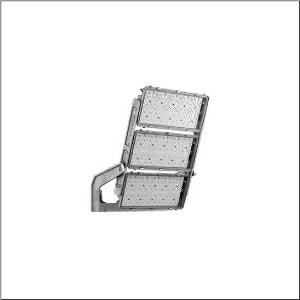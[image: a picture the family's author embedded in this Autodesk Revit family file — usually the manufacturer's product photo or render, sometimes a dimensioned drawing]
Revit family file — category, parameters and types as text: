
# Revit family: floodlight_fl_11_maxi_pro_remote___pl64_5xa779427v01aa_f124
name_source: partatom
category: Lighting Fixtures
units: mm (PartAtom-declared; Revit-internal decimal feet)

## family parameters
Cut with Voids When Loaded = No
Host = Face
Light Source = No
Part Type = Normal
Room Calculation Point = No
Round Connector Dimension = Use Diameter
Shared = No

## types (1)
- --- (1 x LED, 220410 lm, 1540.1 W, 5000K)
    Apparent Load = 1540 VA
    CIE Flux Codes = 28 79 98 100 100
    Color Rendering = 70
    Color Temperature = 5000K
    Default Elevation = 1800 mm
    Description = Floodlight FL 11  maxi  pro Remote floodlight; light control with lens of PMMA; cover panel of toughened safety glass, transparent; light distribution: PL64, asymmetric direct distribution, LEDcolour temperature: 5000K, rated luminous flux: 220.410lm, colour rendering: CRI > 70, light colour: 750; luminous efficacy: 143lm/W; brightness control: DALI 2 (1 DALI address); with terminal, 8-pole, max. 2.5mm², mains connection: 220..240V/380..400V AC, 50/60Hz, surge voltage resistance: line to ground: 10kV, ECG replaceable separately, no afterglow with DALI off / DMX off command, LED unit replaceable without ESD environment, dustproof LED module, dimming range 10..100%; 1540W floodlight with 2x LED unit of diecast aluminium, coated grey; length: 713mm / width: 651mm / height: 338mm; mounting bracket, of diecast aluminium, uncoated, natural, equipment: Power, protection rating (complete): IP66; insulation class (complete): insulation class I (protective earthing); certification: CE, ENEC, VDE; ball protection: ball impact resistance with accessories, impact resistance: IK07; only for outdoor installations, rated ambient temperature 10°C, permissible operating ambient temperature: -40..+30°C, permissible storage temperature: -40..+85°Cpackaging unit: 1 piece

Light Distribution: PL64
    Height = 320 mm
    Lamp = 1 x LED
    Lamp Light Flux = 220410 lm
    Lamp Power = 1540.1 W
    Lamp count = 1
    Length = 1002 mm
    Luminous efficacy = 143 lm/W
    Manufacturer = Siteco
    ModVariant = No
    Model = 5XA779427V01AA
    Mounting Place = Ceiling
    Mounting Type = Surface mounted
    Number of Poles = 1
    OnlyDefault = Yes
    Power Factor = 1
    Product Name = Floodlight FL 11 maxi pro Remote | PL64
    Product group = floodlight | ceiling mounted
    ProductGroupID = 301
    Protection Class = Protection class I
    Protection Degree = IP 66
    RLX_Detail_Level = 1
    RLX_Emergency_Light_Flux = 0 lm
    RLX_Emergency_Type = 0
    RLX_Emergency_Type_DB = No
    RlxData = <blob elided: 52405 chars, md5=19477a9e>
    Socket = socket
    Standby Power = 0 W
    System Light Flux = 220410 lm
    System Power = 1540 W
    Type Comments = factory setting: luminous flux: 100 % | dim-lin: 254 | 1080 mA
    Type Image = l_1349141.jpg
    URL = http://relux.com
    VarID = @adj_109272
    Voltage = 0 V
    Weight = 0.00 kg
    Width = 655 mm

## geometry (parser evidence)
native form markers: Blend x4, Sweep x15
no freeform markers — native parametric forms only
